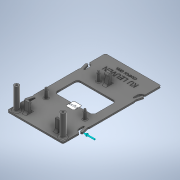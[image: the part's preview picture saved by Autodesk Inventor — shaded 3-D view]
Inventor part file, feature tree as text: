
AUTODESK INVENTOR PART (.ipt)
format: ipt  version: 2022 (Build 260153000, 153)  size: 734,208 bytes
history: native  units: mm
features: sketch x10, extrude x9, fillet x4, plane x3, mirror x3, emboss x1
ambient origin geometry x8: Origin, YZ Plane, XZ Plane, XY Plane, X Axis, Y Axis, Z Axis, Center Point
bodies: Solid1 (feature_tree)
feature tree (30):
  extrude  "Extrusion1"  Depth=127.0mm
  extrude  "Extrusion8"  Depth=4.0mm
  fillet  "Fillet3"  Radius=9.0mm
  extrude  "Extrusion9"  Depth=2.5mm
  fillet  "Fillet4"  Radius=2.5mm
  fillet  "Fillet5"  Radius=2.5mm
  plane  "Work Plane1"
  extrude  "Extrusion11"  Depth=3.0mm
  plane  "Work Plane2"
  mirror  "Mirror1"
  extrude  "Extrusion12"  Depth=2.0mm
  extrude  "Extrusion13"  Depth=29.0mm
  fillet  "Fillet6"  Radius=10.5mm
  extrude  "Extrusion14"  Depth=10.5mm
  emboss  "Emboss2"
  extrude  "Extrusion15"  Depth=11.0mm
  extrude  "Extrusion16"  Depth=10.0mm
  plane  "Work Plane3"
  mirror  "Mirror4"
  mirror  "Mirror5"
  sketch  "Sketch1"  dims[d0=72.0mm d1=127.0mm]
  sketch  "Sketch2"  dims[d2=2.0mm d3=0.0mm d34=4.0mm d62=9.0mm d63=0.0mm]
  sketch  "Sketch8"  dims[d64=1.0mm d65=2.5mm d66=2.5mm d67=2.5mm]
  sketch  "Sketch10"  dims[d68=3.0mm d69=0.0mm d70=0.5mm]
  sketch  "Sketch11"  dims[d82=2.0mm d83=70.0mm]
  sketch  "Sketch12"  dims[d84=82.45mm d85=29.0mm d86=10.5mm]
  sketch  "Sketch13"  dims[d87=25.8mm d88=10.5mm]
  sketch  "Sketch16"  dims[d89=2.3mm d90=11.0mm]
  sketch  "Sketch19"  dims[d91=-16.0mm d92=10.0mm]
  sketch  "Sketch20"  dims[d96=1.0mm d98=3.0mm d100=2.5mm d102=1.5mm d103=3.0mm d105=5.0mm d106=0.0mm d107=10.0mm d109=2.5mm d112=3.0mm d113=3.0mm d115=5.0mm d116=0.0mm d117=10.9mm d118=1.0mm d119=1.5mm d120=10.9mm d121=5.5mm d122=82.45mm d123=27.7mm d124=50.0mm d125=30.0mm d126=50.0mm d127=4.0mm d128=6.0mm d129=6.0mm d130=6.0mm d131=6.0mm d132=6.0mm d133=28.0mm d134=0.0mm d135=2.0mm d136=2.5mm d137=2.5mm d138=10.0mm d139=0.0mm d162=5.0mm d163=1.0mm d164=0.0mm d182=5.0mm d185=20.0mm d188=15.0mm d193=0.0mm d194=0.0mm d195=3.0mm d196=4.0mm d197=3.0mm d199=1.5mm d200=15.0deg d201=6.0mm d202=1.5mm d203=0.0mm d204=0.0mm]
